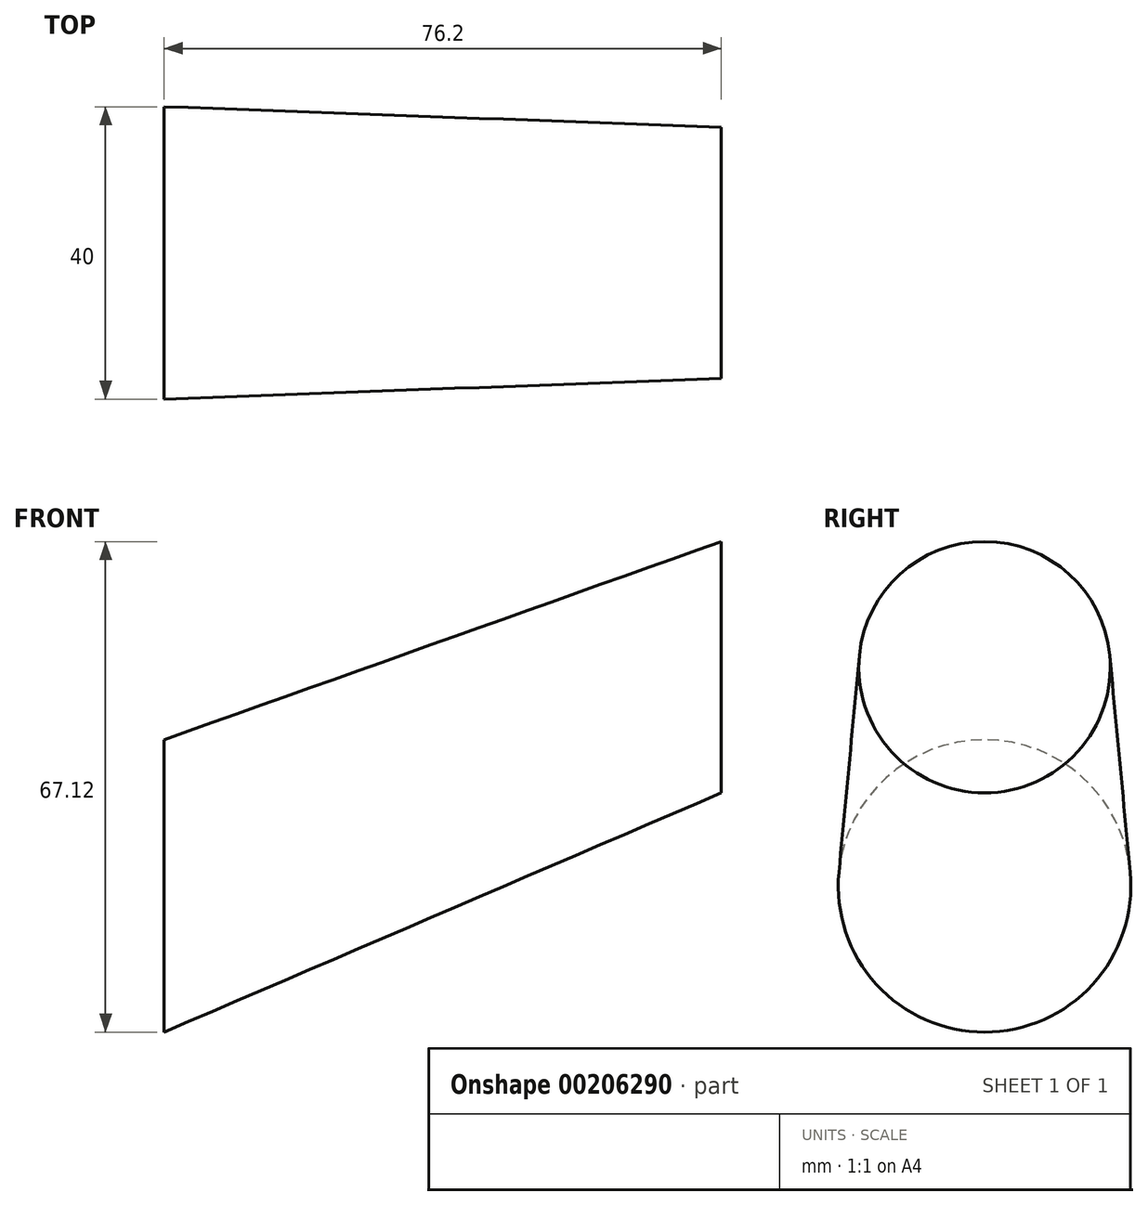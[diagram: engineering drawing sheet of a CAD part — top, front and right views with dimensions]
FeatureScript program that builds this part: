
annotation { "Feature Type Name" : "Feature", "Feature Type Description" : "" }
export const myFeature = defineFeature(function(context is Context, id is Id, definition is map)
    precondition{}
    {
        {
            var Q0;
            Q0=qCreatedBy(makeId("Right.planeOp"),FACE);
            var sketch = newSketch(context, id + "F0", { "sketchPlane" : qUnion([Q0])});
            skCircle(sketch, "E0", {"center": v(0, 0) * mm, "radius": 20 * mm});
            skSolve(sketch);
        }
        {
            var Q0;
            Q0=qCreatedBy(makeId("Right.planeOp"),FACE);
            cPlane(context, id + "F1", {"entities" : qUnion([Q0]), "cplaneType" : CPlaneType.OFFSET, "offset" : 76.2 * mm, "width" : 152.4 * mm, "height" : 152.4 * mm});
        }
        {
            var Q0;
            Q0=qCreatedBy(id+"F1.planeOp",FACE);
            var sketch = newSketch(context, id + "F2", { "sketchPlane" : qUnion([Q0])});
            skCircle(sketch, "E1", {"center": v(0, 29.93) * mm, "radius": 17.2 * mm});
            skSolve(sketch);
        }
        {
            var Q0;
            Q0=makeQuery(id+"F0.imprint","IMPRINT",FACE,{"disambiguationData":[TD([[makeQuery(id+"F0.imprint","IMPRINT",EDGE,{"derivedFrom":sQuery(id+"F0.wireOp",EDGE,"E0")}),1.0]])]});
            var Q1;
            Q1=makeQuery(id+"F2.imprint","IMPRINT",FACE,{"disambiguationData":[TD([[makeQuery(id+"F2.imprint","IMPRINT",EDGE,{"derivedFrom":sQuery(id+"F2.wireOp",EDGE,"E1")}),1.0]])]});
            loft(context, id + "F3", {"sheetProfilesArray" : [{ "sheetProfileEntities" : qUnion([Q0]) }, { "sheetProfileEntities" : qUnion([Q1]) }]});
        }
    });
